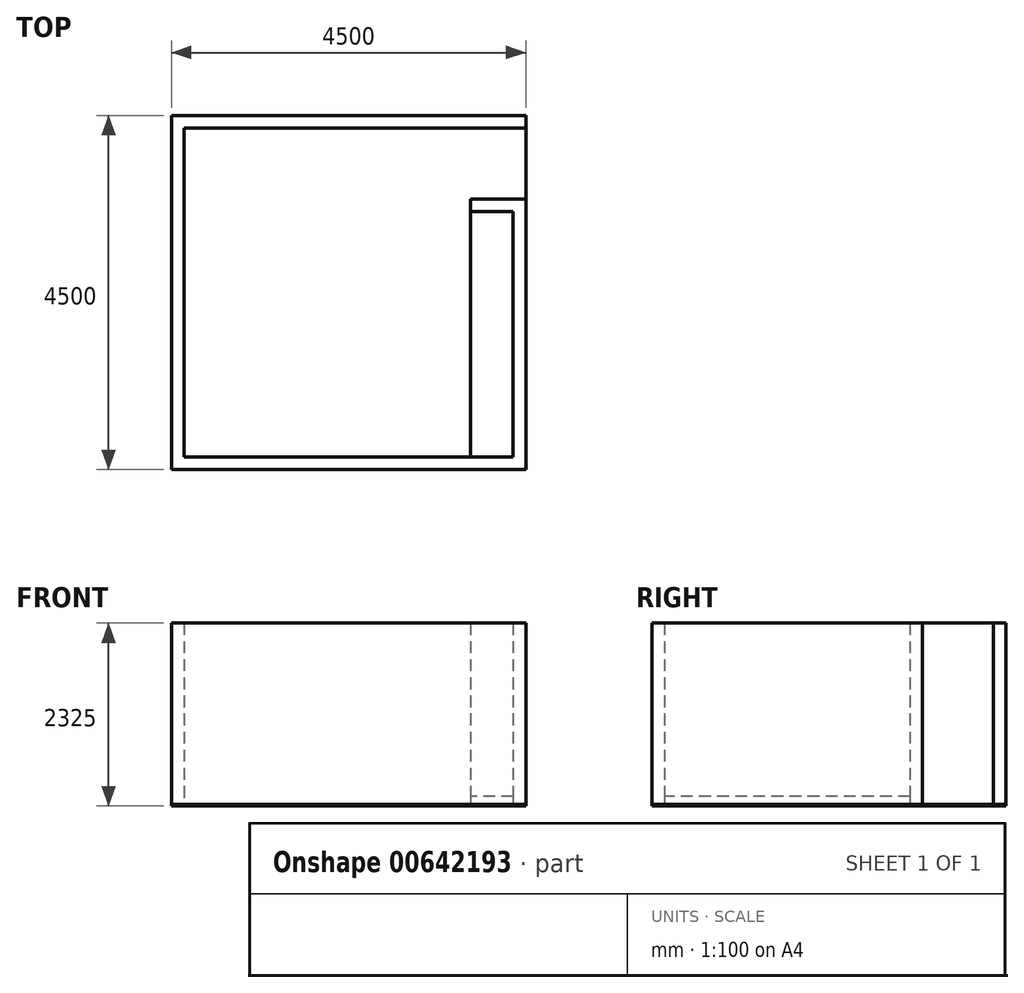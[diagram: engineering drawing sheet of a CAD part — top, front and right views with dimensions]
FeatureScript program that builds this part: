
annotation { "Feature Type Name" : "Feature", "Feature Type Description" : "" }
export const myFeature = defineFeature(function(context is Context, id is Id, definition is map)
    precondition{}
    {
        {
            var Q0;
            Q0=qCreatedBy(makeId("Top.planeOp"),FACE);
            var sketch = newSketch(context, id + "F0", { "sketchPlane" : qUnion([Q0])});
            skLineSegment(sketch, "E0.bottom", {"start": v(-2249.48, 2652.98) * mm, "end": v(2250.52, 2652.98) * mm});
            skLineSegment(sketch, "E0.top", {"start": v(-2249.48, -1847.02) * mm, "end": v(2250.52, -1847.02) * mm});
            skLineSegment(sketch, "E0.left", {"start": v(-2249.48, 2652.98) * mm, "end": v(-2249.48, -1847.02) * mm});
            skLineSegment(sketch, "E0.right", {"start": v(2250.52, 2652.98) * mm, "end": v(2250.52, -1847.02) * mm});
            skSolve(sketch);
        }
        {
            var Q0;
            Q0=makeQuery(id+"F0.imprint","IMPRINT",FACE,{"disambiguationData":[TD([[makeQuery(id+"F0.imprint","IMPRINT",EDGE,{"derivedFrom":sQuery(id+"F0.wireOp",EDGE,"E0.bottom")}),-1.0]])]});
            extrude(context, id + "F1", {"entities" : qUnion([Q0]), "depth" : 25 * mm, "offsetDistance" : 25 * mm});
        }
        {
            var Q0;
            Q0=makeQuery(id+"F1.opExtrude","CAP_FACE",FACE,{"disambiguationData":[OSD([sQuery(id+"F0.wireOp",EDGE,"E0.bottom"),sQuery(id+"F0.wireOp",EDGE,"E0.top"),sQuery(id+"F0.wireOp",EDGE,"E0.left"),sQuery(id+"F0.wireOp",EDGE,"E0.right")])],"isStart":false});
            var sketch = newSketch(context, id + "F2", { "sketchPlane" : qUnion([Q0])});
            skLineSegment(sketch, "E1", {"start": v(2250.52, 2652.98) * mm, "end": v(2250.52, 2492.98) * mm});
            skLineSegment(sketch, "E2", {"start": v(2250.52, 2492.98) * mm, "end": v(-2089.48, 2492.98) * mm});
            skLineSegment(sketch, "E3", {"start": v(-2089.48, 2492.98) * mm, "end": v(-2089.48, -1687.02) * mm});
            skLineSegment(sketch, "E4", {"start": v(-2089.48, -1687.02) * mm, "end": v(2090.52, -1687.02) * mm});
            skLineSegment(sketch, "E5", {"start": v(2090.52, -1687.02) * mm, "end": v(2090.52, 1432.98) * mm});
            skLineSegment(sketch, "E6", {"start": v(2090.52, 1432.98) * mm, "end": v(1550.52, 1432.98) * mm});
            skLineSegment(sketch, "E7", {"start": v(1550.52, 1432.98) * mm, "end": v(1550.52, 1592.98) * mm});
            skLineSegment(sketch, "E8", {"start": v(1550.52, 1592.98) * mm, "end": v(2250.52, 1592.98) * mm});
            skLineSegment(sketch, "E9", {"start": v(2250.52, 1592.98) * mm, "end": v(2250.52, -1847.02) * mm});
            skLineSegment(sketch, "E10", {"start": v(2250.52, -1847.02) * mm, "end": v(-2249.48, -1847.02) * mm});
            skLineSegment(sketch, "E11", {"start": v(-2249.48, -1847.02) * mm, "end": v(-2249.48, 2652.98) * mm});
            skSolve(sketch);
        }
        {
            var Q0;
            Q0=makeQuery(id+"F2.imprint","IMPRINT",FACE,{"disambiguationData":[TD([[makeQuery(id+"F2.imprint","IMPRINT",EDGE,{"derivedFrom":sQuery(id+"F2.wireOp",EDGE,"E1")}),-1.0]])]});
            extrude(context, id + "F3", {"entities" : qUnion([Q0]), "depth" : 2300 * mm, "offsetDistance" : 25 * mm});
        }
        {
            var Q0;
            Q0=makeQuery(id+"F1.opExtrude","CAP_FACE",FACE,{"disambiguationData":[OSD([sQuery(id+"F0.wireOp",EDGE,"E0.bottom"),sQuery(id+"F0.wireOp",EDGE,"E0.top"),sQuery(id+"F0.wireOp",EDGE,"E0.left"),sQuery(id+"F0.wireOp",EDGE,"E0.right")])],"isStart":false});
            var sketch = newSketch(context, id + "F4", { "sketchPlane" : qUnion([Q0])});
            skLineSegment(sketch, "E12.bottom", {"start": v(2090.52, 1432.98) * mm, "end": v(1550.52, 1432.98) * mm});
            skLineSegment(sketch, "E12.top", {"start": v(2090.52, -1687.02) * mm, "end": v(1550.52, -1687.02) * mm});
            skLineSegment(sketch, "E12.left", {"start": v(2090.52, 1432.98) * mm, "end": v(2090.52, -1687.02) * mm});
            skLineSegment(sketch, "E12.right", {"start": v(1550.52, 1432.98) * mm, "end": v(1550.52, -1687.02) * mm});
            skSolve(sketch);
        }
        {
            var Q0;
            Q0 = qSketchRegion(id + "F4", true);
            extrude(context, id + "F5", {"entities" : qUnion([Q0]), "depth" : 100 * mm, "offsetDistance" : 25 * mm});
        }
    });
